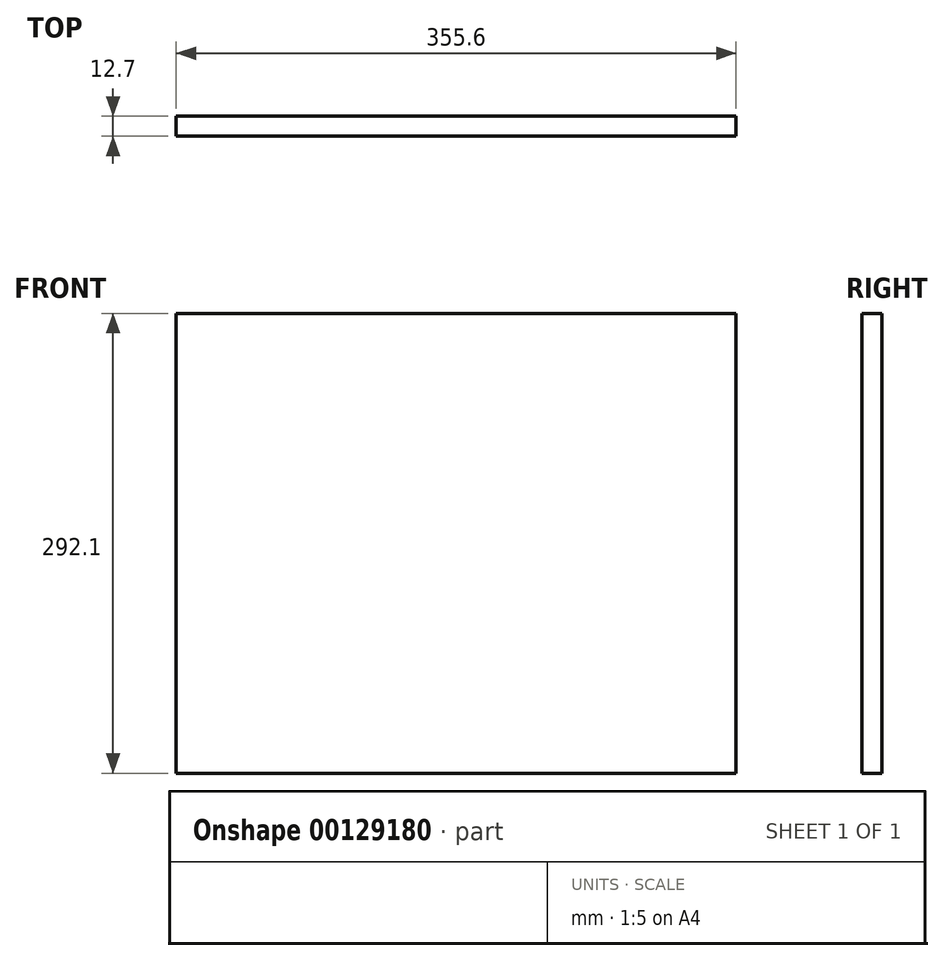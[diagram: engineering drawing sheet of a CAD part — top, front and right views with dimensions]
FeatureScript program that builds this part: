
annotation { "Feature Type Name" : "Feature", "Feature Type Description" : "" }
export const myFeature = defineFeature(function(context is Context, id is Id, definition is map)
    precondition{}
    {
        {
            var Q0;
            Q0=qCreatedBy(makeId("Front.planeOp"),FACE);
            var sketch = newSketch(context, id + "F0", { "sketchPlane" : qUnion([Q0])});
            skLineSegment(sketch, "E0.bottom", {"start": v(-177.8, 146.05) * mm, "end": v(177.8, 146.05) * mm});
            skLineSegment(sketch, "E0.top", {"start": v(-177.8, -146.05) * mm, "end": v(177.8, -146.05) * mm});
            skLineSegment(sketch, "E0.left", {"start": v(-177.8, 146.05) * mm, "end": v(-177.8, -146.05) * mm});
            skLineSegment(sketch, "E0.right", {"start": v(177.8, 146.05) * mm, "end": v(177.8, -146.05) * mm});
            skPoint(sketch, "E0.middle", {"position": v(0, 0) * mm});
            skSolve(sketch);
        }
        {
            var Q0;
            Q0=makeQuery(id+"F0.imprint","IMPRINT",FACE,{"disambiguationData":[TD([[makeQuery(id+"F0.imprint","IMPRINT",EDGE,{"derivedFrom":sQuery(id+"F0.wireOp",EDGE,"E0.bottom")}),-1.0]])]});
            extrude(context, id + "F1", {"entities" : qUnion([Q0]), "depth" : 12.7 * mm});
        }
    });
